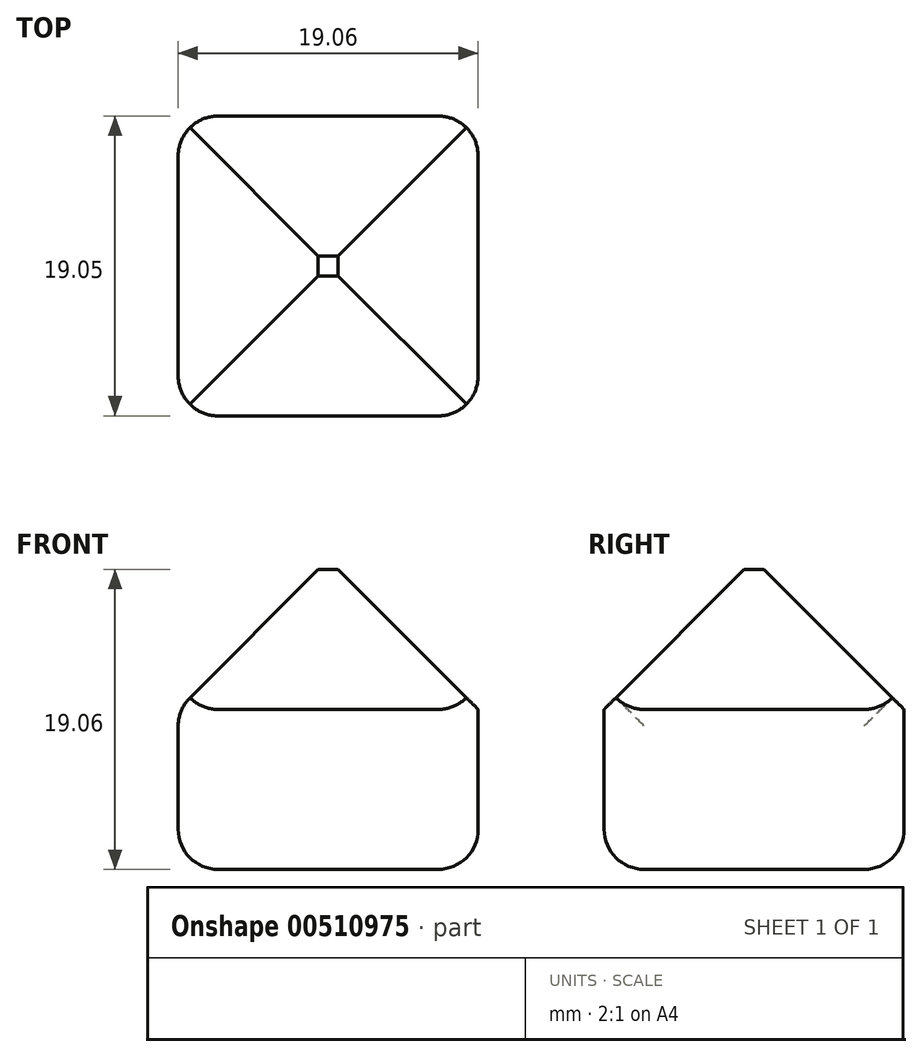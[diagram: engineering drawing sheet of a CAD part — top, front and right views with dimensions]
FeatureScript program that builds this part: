
annotation { "Feature Type Name" : "Feature", "Feature Type Description" : "" }
export const myFeature = defineFeature(function(context is Context, id is Id, definition is map)
    precondition{}
    {
        {
            var Q0;
            Q0=qCreatedBy(makeId("Front.planeOp"),FACE);
            var sketch = newSketch(context, id + "F0", { "sketchPlane" : qUnion([Q0])});
            skLineSegment(sketch, "E0.bottom", {"start": v(9.53, 9.52) * mm, "end": v(-9.53, 9.52) * mm});
            skLineSegment(sketch, "E0.top", {"start": v(9.53, -9.53) * mm, "end": v(-9.53, -9.53) * mm});
            skLineSegment(sketch, "E0.left", {"start": v(9.53, 9.52) * mm, "end": v(9.53, -9.53) * mm});
            skLineSegment(sketch, "E0.right", {"start": v(-9.53, 9.53) * mm, "end": v(-9.53, -9.53) * mm});
            skPoint(sketch, "E0.middle", {"position": v(0, 0) * mm});
            skSolve(sketch);
        }
        {
            var Q0;
            Q0 = qSketchRegion(id + "F0", true);
            extrude(context, id + "F1", {"entities" : qUnion([Q0]), "depth" : 19.05 * mm});
        }
        {
            var Q0;
            Q0=makeQuery(id+"F1.opExtrude","CAP_EDGE",EDGE,{"disambiguationData":[OSD([sQuery(id+"F0.wireOp",EDGE,"E0.bottom")])],"isStart":false});
            var Q1;
            Q1=makeQuery(id+"F1.opExtrude","CAP_EDGE",EDGE,{"disambiguationData":[OSD([sQuery(id+"F0.wireOp",EDGE,"E0.bottom")])],"isStart":true});
            var Q2;
            Q2=makeQuery(id+"F1.opExtrude","SWEPT_EDGE",EDGE,{"disambiguationData":[OSD([sQuery(id+"F0.wireOp",EDGE,"E0.bottom"),sQuery(id+"F0.wireOp",EDGE,"E0.left")])]});
            var Q3;
            Q3=makeQuery(id+"F1.opExtrude","SWEPT_EDGE",EDGE,{"disambiguationData":[OSD([sQuery(id+"F0.wireOp",EDGE,"E0.bottom"),sQuery(id+"F0.wireOp",EDGE,"E0.right")])]});
            chamfer(context, id + "F2", {"entities" : qUnion([Q0, Q1, Q2, Q3]), "width" : 8.9 * mm, "tangentPropagation" : true});
        }
        {
            var Q0;
            Q0=makeQuery(id+"F1.opExtrude","CAP_EDGE",EDGE,{"disambiguationData":[OSD([sQuery(id+"F0.wireOp",EDGE,"E0.left")])],"isStart":false});
            var Q1;
            Q1=makeQuery(id+"F1.opExtrude","CAP_EDGE",EDGE,{"disambiguationData":[OSD([sQuery(id+"F0.wireOp",EDGE,"E0.top")])],"isStart":false});
            var Q2;
            Q2=makeQuery(id+"F1.opExtrude","SWEPT_FACE",FACE,{"disambiguationData":[OSD([sQuery(id+"F0.wireOp",EDGE,"E0.right")])]});
            var Q3;
            Q3=makeQuery(id+"F1.opExtrude","CAP_EDGE",EDGE,{"disambiguationData":[OSD([sQuery(id+"F0.wireOp",EDGE,"E0.left")])],"isStart":true});
            var Q4;
            Q4=makeQuery(id+"F1.opExtrude","SWEPT_FACE",FACE,{"disambiguationData":[OSD([sQuery(id+"F0.wireOp",EDGE,"E0.top")])]});
            var Q5;
            Q5=makeQuery(id+"F1.opExtrude","SWEPT_EDGE",EDGE,{"disambiguationData":[OSD([sQuery(id+"F0.wireOp",EDGE,"E0.top"),sQuery(id+"F0.wireOp",EDGE,"E0.right")])]});
            var Q6;
            {var subQ0=sQuery(id+"F0.wireOp",EDGE,"E0.right");Q6=makeQuery(id+"F2.opChamfer","BLEND_EDGE",EDGE,{"blendedFrom":[makeQuery(id+"F1.opExtrude","SWEPT_EDGE",EDGE,{"disambiguationData":[OSD([sQuery(id+"F0.wireOp",EDGE,"E0.bottom"),subQ0])]}),makeQuery(id+"F1.opExtrude","SWEPT_FACE",FACE,{"disambiguationData":[OSD([subQ0])]})],"blendedInto":[makeQuery(id+"F1.opExtrude","SWEPT_FACE",FACE,{"disambiguationData":[OSD([subQ0])]})]});}
            fillet(context, id + "F3", {"entities" : qUnion([Q0, Q1, Q2, Q3, Q4, Q5, Q6]), "radius" : 2.54 * mm, "tangentPropagation" : true, "allowEdgeOverflow" : false});
        }
    });
